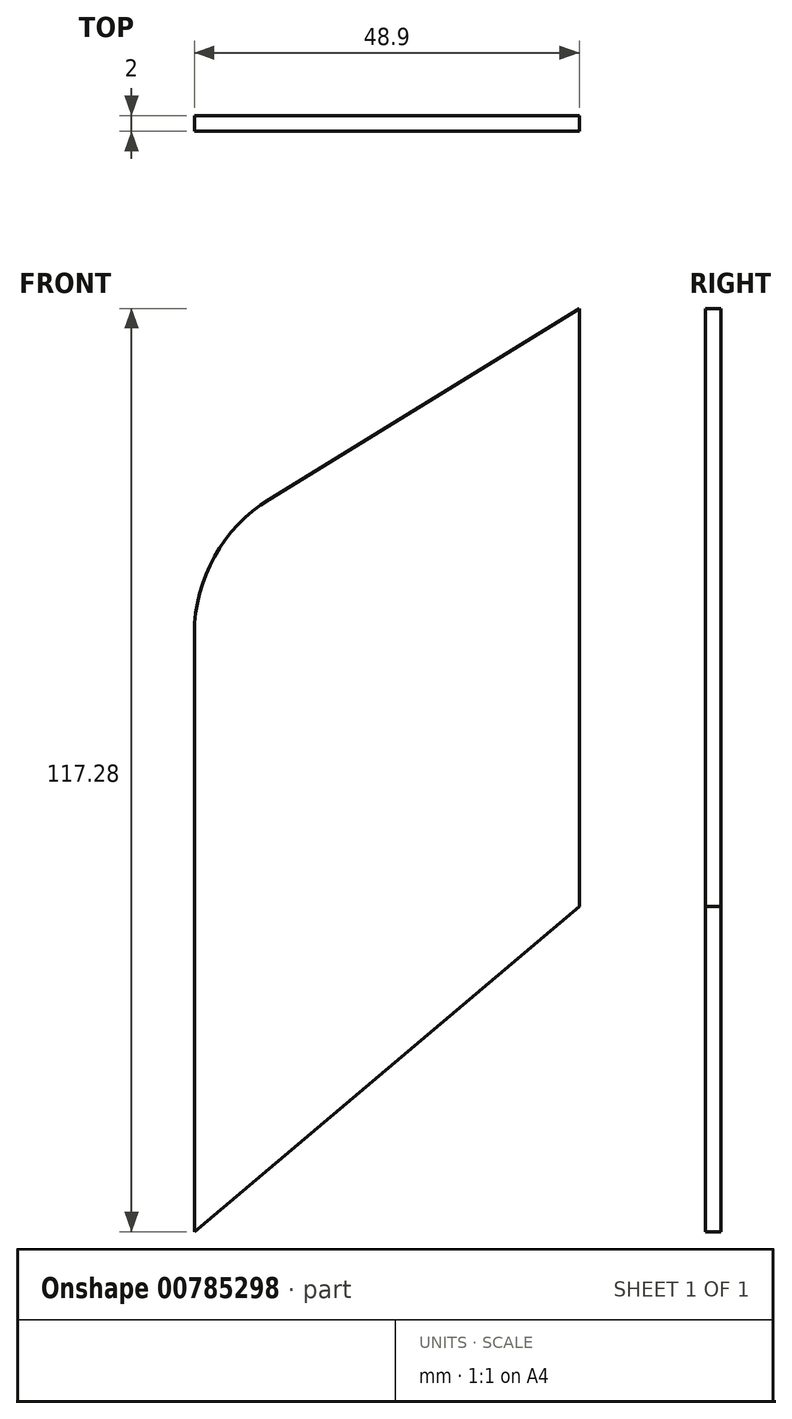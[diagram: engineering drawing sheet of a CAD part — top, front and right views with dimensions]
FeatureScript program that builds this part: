
annotation { "Feature Type Name" : "Feature", "Feature Type Description" : "" }
export const myFeature = defineFeature(function(context is Context, id is Id, definition is map)
    precondition{}
    {
        {
            var Q0;
            Q0=qCreatedBy(makeId("Front.planeOp"),FACE);
            var sketch = newSketch(context, id + "F0", { "sketchPlane" : qUnion([Q0])});
            skLineSegment(sketch, "E0", {"start": v(0, 58.61) * mm, "end": v(0, -17.39) * mm});
            skLineSegment(sketch, "E1", {"start": v(0, -17.39) * mm, "end": v(-48.9, -58.67) * mm});
            skLineSegment(sketch, "E2", {"start": v(-48.9, -58.67) * mm, "end": v(-48.9, 17.33) * mm});
            skLineSegment(sketch, "E3", {"start": v(-39.39, 34.36) * mm, "end": v(0, 58.61) * mm});
            skPoint(sketch, "E4.visualSharp", {"position": v(-48.9, 28.5) * mm});
            skArc(sketch, "E4.filletArc", {"start": v(-39.39, 34.36) * mm, "mid": v(-46.36, 27.08) * mm, "end": v(-48.9, 17.33) * mm});
            skSolve(sketch);
        }
        {
            var Q0;
            Q0 = qSketchRegion(id + "F0", true);
            extrude(context, id + "F1", {"entities" : qUnion([Q0]), "depth" : 2 * mm, "offsetDistance" : 25.4 * mm});
        }
    });
